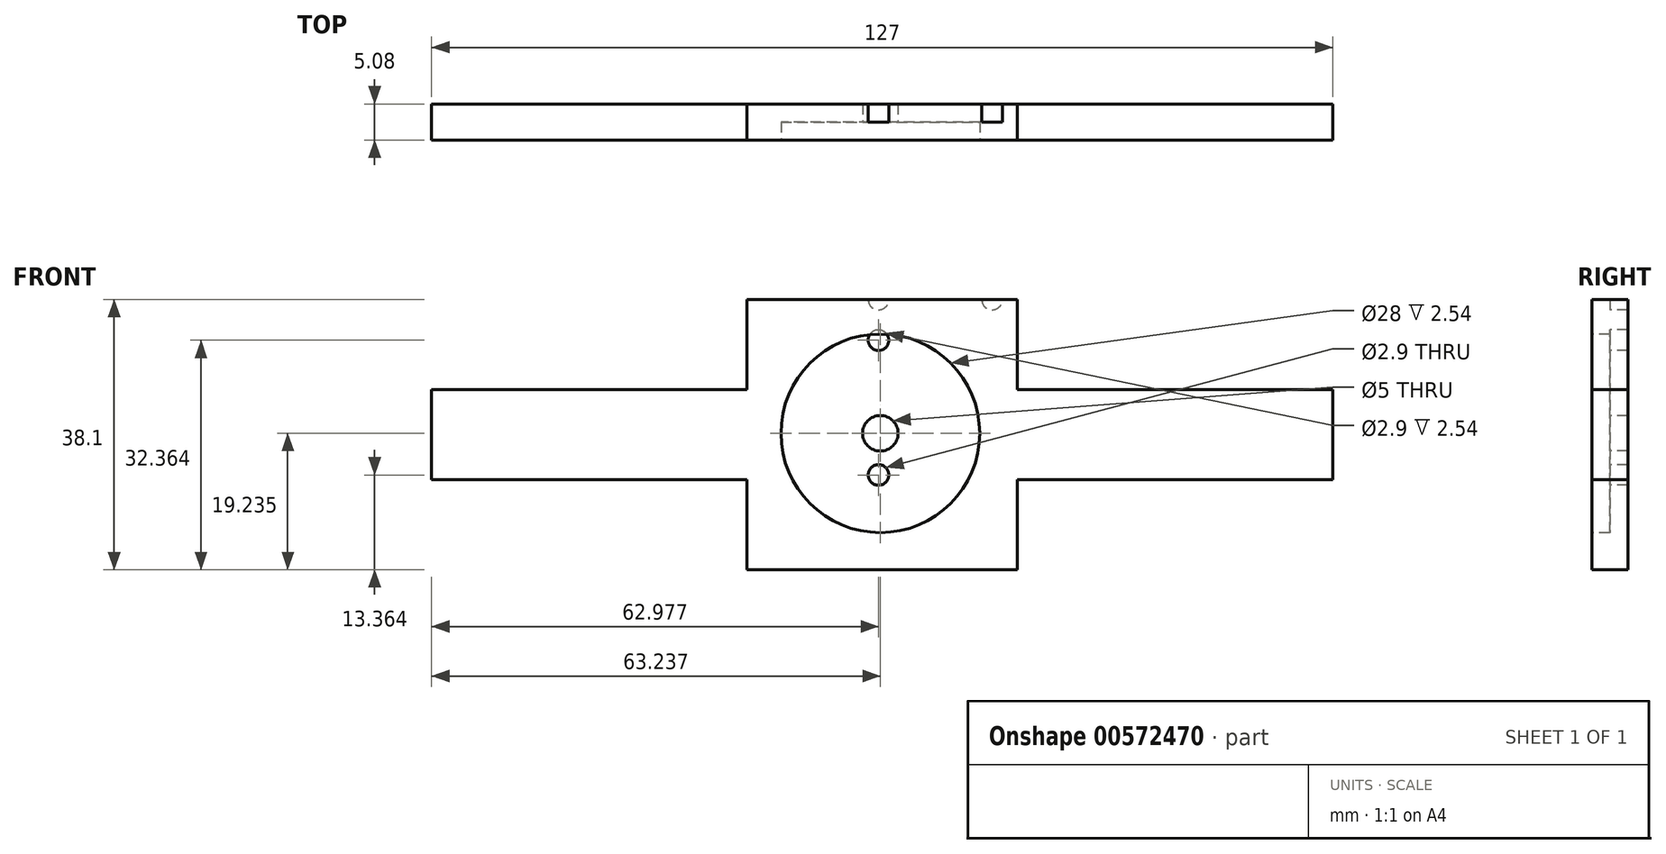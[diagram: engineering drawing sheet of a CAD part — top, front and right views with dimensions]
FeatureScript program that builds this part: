
annotation { "Feature Type Name" : "Feature", "Feature Type Description" : "" }
export const myFeature = defineFeature(function(context is Context, id is Id, definition is map)
    precondition{}
    {
        {
            var Q0;
            Q0=qCreatedBy(makeId("Front.planeOp"),FACE);
            var sketch = newSketch(context, id + "F0", { "sketchPlane" : qUnion([Q0])});
            skLineSegment(sketch, "E0.bottom", {"start": v(-61.14, -2.4) * mm, "end": v(65.86, -2.4) * mm});
            skLineSegment(sketch, "E0.top", {"start": v(-61.14, -15.1) * mm, "end": v(65.86, -15.1) * mm});
            skLineSegment(sketch, "E0.left", {"start": v(-61.14, -2.4) * mm, "end": v(-61.14, -15.1) * mm});
            skLineSegment(sketch, "E0.right", {"start": v(65.86, -2.4) * mm, "end": v(65.86, -15.1) * mm});
            skLineSegment(sketch, "E1.bottom", {"start": v(-16.69, 10.3) * mm, "end": v(21.41, 10.3) * mm});
            skLineSegment(sketch, "E1.top", {"start": v(-16.69, -27.8) * mm, "end": v(21.41, -27.8) * mm});
            skLineSegment(sketch, "E1.left", {"start": v(-16.69, 10.3) * mm, "end": v(-16.69, -27.8) * mm});
            skLineSegment(sketch, "E1.right", {"start": v(21.41, 10.3) * mm, "end": v(21.41, -27.8) * mm});
            skLineSegment(sketch, "E2.bottom", {"start": v(42.14, -2.4) * mm, "end": v(54.84, -2.4) * mm});
            skLineSegment(sketch, "E2.top", {"start": v(42.14, -15.1) * mm, "end": v(54.84, -15.1) * mm});
            skLineSegment(sketch, "E2.left", {"start": v(42.14, -2.4) * mm, "end": v(42.14, -15.1) * mm});
            skLineSegment(sketch, "E2.right", {"start": v(54.84, -2.4) * mm, "end": v(54.84, -15.1) * mm});
            skSolve(sketch);
        }
        {
            var Q0;
            Q0=qSketchRegion(id+"F0",true);
            extrude(context, id + "F1", {"entities" : qUnion([Q0]), "depth" : 5.08 * mm, "offsetDistance" : 25.4 * mm});
        }
        {
            var Q0;
            Q0=makeQuery(id+"F1.opExtrude","CAP_FACE",FACE,{"disambiguationData":[OSD([sQuery(id+"F0.wireOp",EDGE,"E0.bottom"),sQuery(id+"F0.wireOp",EDGE,"E0.top"),sQuery(id+"F0.wireOp",EDGE,"E0.left"),sQuery(id+"F0.wireOp",EDGE,"E0.right"),sQuery(id+"F0.wireOp",EDGE,"E1.bottom"),sQuery(id+"F0.wireOp",EDGE,"E1.top"),sQuery(id+"F0.wireOp",EDGE,"E1.left"),sQuery(id+"F0.wireOp",EDGE,"E1.right")])],"isStart":false});
            var sketch = newSketch(context, id + "F2", { "sketchPlane" : qUnion([Q0])});
            skCircle(sketch, "E3", {"center": v(2.1, -8.57) * mm, "radius": 14 * mm});
            skSolve(sketch);
        }
        {
            var Q0;
            Q0=makeQuery(id+"F2.imprint","IMPRINT",FACE,{"disambiguationData":[TD([[makeQuery(id+"F2.imprint","IMPRINT",EDGE,{"derivedFrom":sQuery(id+"F2.wireOp",EDGE,"E3")}),1.0]])]});
            extrude(context, id + "F3", {"entities" : qUnion([Q0]), "operationType" : NewBodyOperationType.REMOVE, "oppositeDirection" : true, "depth" : 2.54 * mm, "offsetDistance" : 25.4 * mm});
        }
        {
            var Q0;
            Q0=makeQuery(id+"F3.boolean.opBoolean","COPY",FACE,{"derivedFrom":makeQuery(id+"F3.opExtrude","CAP_FACE",FACE,{"disambiguationData":[OSD([sQuery(id+"F2.wireOp",EDGE,"E3")])],"isStart":false})});
            var sketch = newSketch(context, id + "F4", { "sketchPlane" : qUnion([Q0])});
            skCircle(sketch, "E4", {"center": v(17.84, 10.3) * mm, "radius": 1.45 * mm});
            skCircle(sketch, "E5", {"center": v(1.84, 10.3) * mm, "radius": 1.45 * mm});
            skCircle(sketch, "E6", {"center": v(1.84, -14.44) * mm, "radius": 1.45 * mm});
            skCircle(sketch, "E7", {"center": v(1.84, 4.56) * mm, "radius": 1.45 * mm});
            skCircle(sketch, "E8", {"center": v(2.1, -8.57) * mm, "radius": 2.5 * mm});
            skPoint(sketch, "E9", {"position": v(-52.37, 10.3) * mm});
            skSolve(sketch);
        }
        {
            var Q0;
            Q0=qSketchRegion(id+"F4",true);
            extrude(context, id + "F5", {"entities" : qUnion([Q0]), "operationType" : NewBodyOperationType.REMOVE, "oppositeDirection" : true, "depth" : 25.4 * mm, "offsetDistance" : 25.4 * mm});
        }
    });
